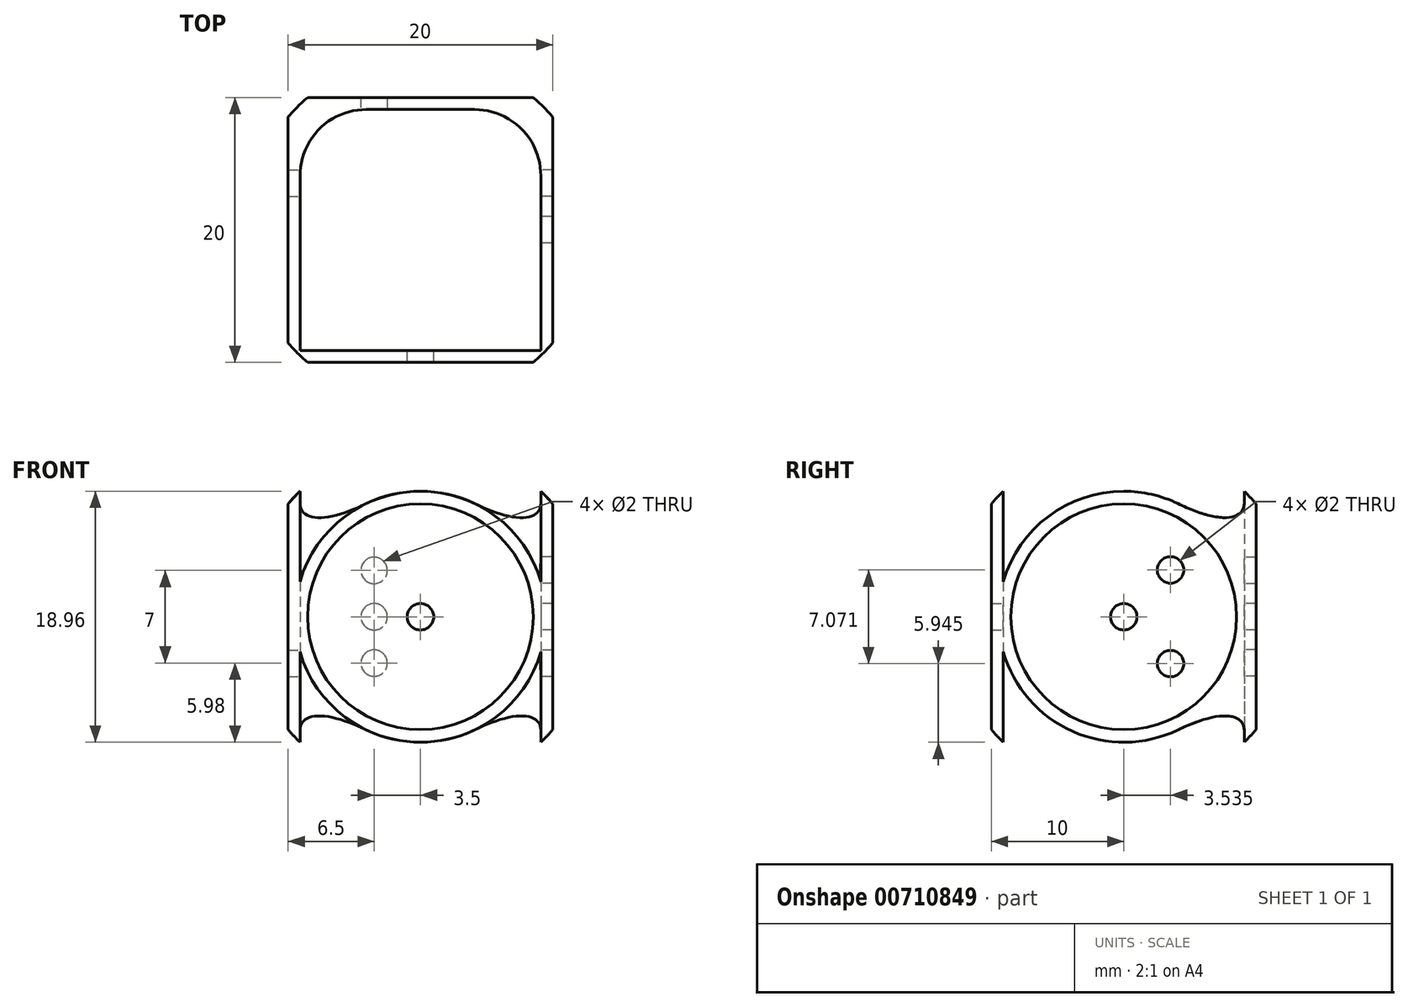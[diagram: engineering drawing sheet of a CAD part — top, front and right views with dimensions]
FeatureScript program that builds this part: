
annotation { "Feature Type Name" : "Feature", "Feature Type Description" : "" }
export const myFeature = defineFeature(function(context is Context, id is Id, definition is map)
    precondition{}
    {
        {
            assignVariable(context, id + "F0", {"name" : "length", "anyValue" : 20 * mm});
        }
        {
            var Q0;
            Q0=qCreatedBy(makeId("Top.planeOp"),FACE);
            var sketch = newSketch(context, id + "F1", { "sketchPlane" : qUnion([Q0])});
            skLineSegment(sketch, "E0.bottom", {"start": v(10, -10) * mm, "end": v(-10, -10) * mm});
            skLineSegment(sketch, "E0.top", {"start": v(10, 10) * mm, "end": v(-10, 10) * mm});
            skLineSegment(sketch, "E0.left", {"start": v(10, -10) * mm, "end": v(10, 10) * mm});
            skLineSegment(sketch, "E0.right", {"start": v(-10, -10) * mm, "end": v(-10, 10) * mm});
            skPoint(sketch, "E0.middle", {"position": v(0, 0) * mm});
            skCircle(sketch, "E1", {"center": v(0, 0) * mm, "radius": 13.14 * mm});
            skCircle(sketch, "E2", {"center": v(0, 0) * mm, "radius": 20 * mm});
            skLineSegment(sketch, "E3", {"start": v(-20, 0) * mm, "end": v(20, 0) * mm});
            skLineSegment(sketch, "E4", {"start": v(-10, 0) * mm, "end": v(-9, 0) * mm, "construction": true});
            skLineSegment(sketch, "E5", {"start": v(9, 0) * mm, "end": v(10, 0) * mm, "construction": true});
            skLineSegment(sketch, "E6.bottom", {"start": v(-9, 0) * mm, "end": v(9, 0) * mm});
            skLineSegment(sketch, "E7", {"start": v(-10, -10) * mm, "end": v(0, 0) * mm, "construction": true});
            skLineSegment(sketch, "E8", {"start": v(0, 0) * mm, "end": v(10, -10) * mm, "construction": true});
            skLineSegment(sketch, "E9.0", {"start": v(4.1, 9.1) * mm, "end": v(-4.1, 9.1) * mm});
            skLineSegment(sketch, "E9.1", {"start": v(9.1, -9.1) * mm, "end": v(9.1, 4.1) * mm});
            skLineSegment(sketch, "E9.2", {"start": v(9.1, -9.1) * mm, "end": v(-9.1, -9.1) * mm});
            skLineSegment(sketch, "E9.3", {"start": v(-9.1, -9.1) * mm, "end": v(-9.1, 4.1) * mm});
            skPoint(sketch, "E10.visualSharp", {"position": v(-9.1, 9.1) * mm});
            skArc(sketch, "E10.filletArc", {"start": v(-4.1, 9.1) * mm, "mid": v(-7.64, 7.64) * mm, "end": v(-9.1, 4.1) * mm});
            skPoint(sketch, "E11.visualSharp", {"position": v(9.1, 9.1) * mm});
            skArc(sketch, "E11.filletArc", {"start": v(9.1, 4.1) * mm, "mid": v(7.64, 7.64) * mm, "end": v(4.1, 9.1) * mm});
            skLineSegment(sketch, "E12.bottom", {"start": v(-9.1, -9.1) * mm, "end": v(9.1, -9.1) * mm});
            skLineSegment(sketch, "E12.top", {"start": v(-9.1, -4) * mm, "end": v(9.1, -4) * mm});
            skLineSegment(sketch, "E12.left", {"start": v(-9.1, -9.1) * mm, "end": v(-9.1, -4) * mm});
            skLineSegment(sketch, "E12.right", {"start": v(9.1, -9.1) * mm, "end": v(9.1, -4) * mm});
            skLineSegment(sketch, "E13.top", {"start": v(-9.1, -2) * mm, "end": v(9.1, -2) * mm});
            skLineSegment(sketch, "E13.left", {"start": v(-9.1, -4) * mm, "end": v(-9.1, -2) * mm});
            skLineSegment(sketch, "E13.right", {"start": v(9.1, -4) * mm, "end": v(9.1, -2) * mm});
            skLineSegment(sketch, "E14", {"start": v(0, 9.1) * mm, "end": v(0, -9.1) * mm});
            skSolve(sketch);
        }
        {
            var Q0;
            Q0=makeQuery(id+"F1.imprint","IMPRINT",FACE,{"disambiguationData":[TD([[makeQuery(id+"F1.imprint","IMPRINT",EDGE,{"derivedFrom":sQuery(id+"F1.wireOp",EDGE,"E0.bottom")}),-1.0]])]});
            var Q1;
            {var subQ0=sQuery(id+"F1.wireOp",EDGE,"Hq5PeDMM-4LUm-VwHA-vir1-N3C3vIOzQR29");var subQ1=sQuery(id+"F1.wireOp",EDGE,"E0.right");var subQ8=makeQuery(id+"F1.imprint","INTERSECT",VERTEX,{"disambiguationData":[OD(0.0)],"derivedFrom":[subQ1,subQ0]});Q1=makeQuery(id+"F1.imprint","IMPRINT",FACE,{"disambiguationData":[TD([[makeQuery(id+"F1.imprint","IMPRINT",EDGE,{"disambiguationData":[TD([[subQ8,-1.0]])],"derivedFrom":subQ1}),-1.0]])]});}
            var Q2;
            {var subQ1=sQuery(id+"F1.wireOp",EDGE,"E0.left");var subQ3=sQuery(id+"F1.wireOp",EDGE,"Hq5PeDMM-4LUm-VwHA-vir1-N3C3vIOzQR29");var subQ4=makeQuery(id+"F1.imprint","INTERSECT",VERTEX,{"disambiguationData":[OD(0.0)],"derivedFrom":[subQ1,subQ3]});Q2=makeQuery(id+"F1.imprint","IMPRINT",FACE,{"disambiguationData":[TD([[makeQuery(id+"F1.imprint","IMPRINT",EDGE,{"disambiguationData":[TD([[subQ4,1.0]])],"derivedFrom":subQ3}),-1.0]])]});}
            var Q3;
            {var subQ0=sQuery(id+"F1.wireOp",EDGE,"Hq5PeDMM-4LUm-VwHA-vir1-N3C3vIOzQR29");var subQ1=sQuery(id+"F1.wireOp",EDGE,"E0.left");var subQ7=makeQuery(id+"F1.imprint","INTERSECT",VERTEX,{"disambiguationData":[OD(0.0)],"derivedFrom":[subQ1,subQ0]});Q3=makeQuery(id+"F1.imprint","IMPRINT",FACE,{"disambiguationData":[TD([[makeQuery(id+"F1.imprint","IMPRINT",EDGE,{"disambiguationData":[TD([[subQ7,-1.0]])],"derivedFrom":subQ1}),1.0]])]});}
            var Q4;
            {var subQ1=sQuery(id+"F1.wireOp",EDGE,"E0.right");var subQ3=sQuery(id+"F1.wireOp",EDGE,"Hq5PeDMM-4LUm-VwHA-vir1-N3C3vIOzQR29");var subQ4=makeQuery(id+"F1.imprint","INTERSECT",VERTEX,{"disambiguationData":[OD(0.0)],"derivedFrom":[subQ1,subQ3]});Q4=makeQuery(id+"F1.imprint","IMPRINT",FACE,{"disambiguationData":[TD([[makeQuery(id+"F1.imprint","IMPRINT",EDGE,{"disambiguationData":[TD([[subQ4,-1.0]])],"derivedFrom":subQ3}),-1.0]])]});}
            var Q5;
            {var subQ0=sQuery(id+"F1.wireOp",EDGE,"Hq5PeDMM-4LUm-VwHA-vir1-N3C3vIOzQR29");var subQ1=sQuery(id+"F1.wireOp",EDGE,"E0.top");var subQ2=makeQuery(id+"F1.imprint","INTERSECT",VERTEX,{"disambiguationData":[OD(0.0)],"derivedFrom":[subQ1,subQ0]});Q5=makeQuery(id+"F1.imprint","IMPRINT",FACE,{"disambiguationData":[TD([[makeQuery(id+"F1.imprint","IMPRINT",EDGE,{"disambiguationData":[TD([[subQ2,-1.0]])],"derivedFrom":subQ1}),1.0]])]});}
            var Q6;
            {var subQ1=sQuery(id+"F1.wireOp",EDGE,"E0.top");var subQ3=sQuery(id+"F1.wireOp",EDGE,"Hq5PeDMM-4LUm-VwHA-vir1-N3C3vIOzQR29");var subQ4=makeQuery(id+"F1.imprint","INTERSECT",VERTEX,{"disambiguationData":[OD(1.0)],"derivedFrom":[subQ1,subQ3]});Q6=makeQuery(id+"F1.imprint","IMPRINT",FACE,{"disambiguationData":[TD([[makeQuery(id+"F1.imprint","IMPRINT",EDGE,{"disambiguationData":[TD([[subQ4,-1.0]])],"derivedFrom":subQ3}),-1.0]])]});}
            var Q7;
            {var subQ1=sQuery(id+"F1.wireOp",EDGE,"E0.right");var subQ3=sQuery(id+"F1.wireOp",EDGE,"Hq5PeDMM-4LUm-VwHA-vir1-N3C3vIOzQR29");var subQ4=makeQuery(id+"F1.imprint","INTERSECT",VERTEX,{"disambiguationData":[OD(1.0)],"derivedFrom":[subQ1,subQ3]});Q7=makeQuery(id+"F1.imprint","IMPRINT",FACE,{"disambiguationData":[TD([[makeQuery(id+"F1.imprint","IMPRINT",EDGE,{"disambiguationData":[TD([[subQ4,1.0]])],"derivedFrom":subQ3}),-1.0]])]});}
            var Q8;
            {var subQ1=sQuery(id+"F1.wireOp",EDGE,"E0.top");var subQ3=sQuery(id+"F1.wireOp",EDGE,"Hq5PeDMM-4LUm-VwHA-vir1-N3C3vIOzQR29");var subQ4=makeQuery(id+"F1.imprint","INTERSECT",VERTEX,{"disambiguationData":[OD(0.0)],"derivedFrom":[subQ1,subQ3]});Q8=makeQuery(id+"F1.imprint","IMPRINT",FACE,{"disambiguationData":[TD([[makeQuery(id+"F1.imprint","IMPRINT",EDGE,{"disambiguationData":[TD([[subQ4,1.0]])],"derivedFrom":subQ3}),-1.0]])]});}
            var Q9;
            {var subQ1=sQuery(id+"F1.wireOp",EDGE,"E0.left");var subQ3=sQuery(id+"F1.wireOp",EDGE,"Hq5PeDMM-4LUm-VwHA-vir1-N3C3vIOzQR29");var subQ4=makeQuery(id+"F1.imprint","INTERSECT",VERTEX,{"disambiguationData":[OD(1.0)],"derivedFrom":[subQ1,subQ3]});Q9=makeQuery(id+"F1.imprint","IMPRINT",FACE,{"disambiguationData":[TD([[makeQuery(id+"F1.imprint","IMPRINT",EDGE,{"disambiguationData":[TD([[subQ4,-1.0]])],"derivedFrom":subQ3}),-1.0]])]});}
            var Q10;
            {var subQ0=sQuery(id+"F1.wireOp",EDGE,"Hq5PeDMM-4LUm-VwHA-vir1-N3C3vIOzQR29");var subQ1=sQuery(id+"F1.wireOp",EDGE,"E0.bottom");var subQ8=makeQuery(id+"F1.imprint","INTERSECT",VERTEX,{"disambiguationData":[OD(0.0)],"derivedFrom":[subQ1,subQ0]});Q10=makeQuery(id+"F1.imprint","IMPRINT",FACE,{"disambiguationData":[TD([[makeQuery(id+"F1.imprint","IMPRINT",EDGE,{"disambiguationData":[TD([[subQ8,-1.0]])],"derivedFrom":subQ1}),-1.0]])]});}
            var Q11;
            {var subQ0=sQuery(id+"F1.wireOp",EDGE,"E1");var subQ1=sQuery(id+"F1.wireOp",EDGE,"E0.bottom");var subQ10=makeQuery(id+"F1.imprint","INTERSECT",VERTEX,{"disambiguationData":[OD(0.0)],"derivedFrom":[subQ1,subQ0]});Q11=makeQuery(id+"F1.imprint","IMPRINT",FACE,{"disambiguationData":[TD([[makeQuery(id+"F1.imprint","IMPRINT",EDGE,{"disambiguationData":[TD([[subQ10,-1.0]])],"derivedFrom":subQ1}),-1.0]])]});}
            var Q12;
            {var subQ0=sQuery(id+"F1.wireOp",EDGE,"E1");var subQ1=sQuery(id+"F1.wireOp",EDGE,"E0.top");var subQ2=makeQuery(id+"F1.imprint","INTERSECT",VERTEX,{"disambiguationData":[OD(0.0)],"derivedFrom":[subQ1,subQ0]});Q12=makeQuery(id+"F1.imprint","IMPRINT",FACE,{"disambiguationData":[TD([[makeQuery(id+"F1.imprint","IMPRINT",EDGE,{"disambiguationData":[TD([[subQ2,-1.0]])],"derivedFrom":subQ1}),1.0]])]});}
            var Q13;
            {var subQ0=sQuery(id+"F1.wireOp",EDGE,"E0.right");var subQ1=sQuery(id+"F1.wireOp",EDGE,"E0.top");var subQ2=makeQuery(id+"F1.imprint","INTERSECT",VERTEX,{"derivedFrom":[subQ1,subQ0]});Q13=makeQuery(id+"F1.imprint","IMPRINT",FACE,{"disambiguationData":[TD([[makeQuery(id+"F1.imprint","IMPRINT",EDGE,{"disambiguationData":[TD([[subQ2,1.0]])],"derivedFrom":subQ1}),1.0]])]});}
            var Q14;
            {var subQ0=sQuery(id+"F1.wireOp",EDGE,"E0.left");var subQ1=sQuery(id+"F1.wireOp",EDGE,"E0.top");var subQ2=makeQuery(id+"F1.imprint","INTERSECT",VERTEX,{"derivedFrom":[subQ1,subQ0]});Q14=makeQuery(id+"F1.imprint","IMPRINT",FACE,{"disambiguationData":[TD([[makeQuery(id+"F1.imprint","IMPRINT",EDGE,{"disambiguationData":[TD([[subQ2,-1.0]])],"derivedFrom":subQ1}),1.0]])]});}
            var Q15;
            {var subQ0=sQuery(id+"F1.wireOp",EDGE,"patfPrjC-I4Qt-dAkN-TGbB-FqZXeeQMi0Ai");Q15=makeQuery(id+"F1.imprint","IMPRINT",FACE,{"disambiguationData":[TD([[makeQuery(id+"F1.imprint","IMPRINT",EDGE,{"derivedFrom":subQ0}),1.0]])]});}
            var Q16;
            Q16=makeQuery(id+"F1.imprint","IMPRINT",FACE,{"disambiguationData":[TD([[makeQuery(id+"F1.imprint","IMPRINT",EDGE,{"derivedFrom":sQuery(id+"F1.wireOp",EDGE,"E6.bottom")}),1.0]])]});
            var Q17;
            Q17=makeQuery(id+"F1.imprint","IMPRINT",FACE,{"disambiguationData":[TD([[makeQuery(id+"F1.imprint","IMPRINT",EDGE,{"derivedFrom":sQuery(id+"F1.wireOp",EDGE,"E6.bottom")}),-1.0]])]});
            var Q18;
            {var subQ0=sQuery(id+"F1.wireOp",EDGE,"iiYfwUfe-HNib-MqOO-iY6M-OHTfmbP10WrW");var subQ5=sQuery(id+"F1.wireOp",EDGE,"jVtNNkBl-UzNA-jzoa-2J3p-JG0xdHmN4cFF");var subQ6=makeQuery(id+"F1.imprint","INTERSECT",VERTEX,{"derivedFrom":[subQ0,subQ5]});Q18=makeQuery(id+"F1.imprint","IMPRINT",FACE,{"disambiguationData":[TD([[makeQuery(id+"F1.imprint","IMPRINT",EDGE,{"disambiguationData":[TD([[subQ6,1.0]])],"derivedFrom":subQ5}),-1.0]])]});}
            var Q19;
            {var subQ0=sQuery(id+"F1.wireOp",EDGE,"E6.left");Q19=makeQuery(id+"F1.imprint","IMPRINT",FACE,{"disambiguationData":[TD([[makeQuery(id+"F1.imprint","IMPRINT",EDGE,{"derivedFrom":subQ0}),-1.0]])]});}
            var Q20;
            {var subQ1=sQuery(id+"F1.wireOp",EDGE,"E6.right");Q20=makeQuery(id+"F1.imprint","IMPRINT",FACE,{"disambiguationData":[TD([[makeQuery(id+"F1.imprint","IMPRINT",EDGE,{"derivedFrom":subQ1}),1.0]])]});}
            var Q21;
            {var subQ0=sQuery(id+"F1.wireOp",EDGE,"iiYfwUfe-HNib-MqOO-iY6M-OHTfmbP10WrW");var subQ5=sQuery(id+"F1.wireOp",EDGE,"jVtNNkBl-UzNA-jzoa-2J3p-JG0xdHmN4cFF");var subQ6=makeQuery(id+"F1.imprint","INTERSECT",VERTEX,{"derivedFrom":[subQ0,subQ5]});Q21=makeQuery(id+"F1.imprint","IMPRINT",FACE,{"disambiguationData":[TD([[makeQuery(id+"F1.imprint","IMPRINT",EDGE,{"disambiguationData":[TD([[subQ6,1.0]])],"derivedFrom":subQ5}),1.0]])]});}
            var Q22;
            Q22=makeQuery(id+"F1.imprint","IMPRINT",FACE,{"disambiguationData":[TD([[makeQuery(id+"F1.imprint","IMPRINT",EDGE,{"derivedFrom":sQuery(id+"F1.wireOp",EDGE,"E12.bottom")}),1.0]])]});
            var Q23;
            {var subQ0=sQuery(id+"F1.wireOp",EDGE,"E13.left");Q23=makeQuery(id+"F1.imprint","IMPRINT",FACE,{"disambiguationData":[TD([[makeQuery(id+"F1.imprint","IMPRINT",EDGE,{"derivedFrom":subQ0}),-1.0]])]});}
            var Q24;
            {var subQ0=sQuery(id+"F1.wireOp",EDGE,"E13.right");Q24=makeQuery(id+"F1.imprint","IMPRINT",FACE,{"disambiguationData":[TD([[makeQuery(id+"F1.imprint","IMPRINT",EDGE,{"derivedFrom":subQ0}),1.0]])]});}
            extrude(context, id + "F2", {"entities" : qUnion([Q0, Q1, Q2, Q3, Q4, Q5, Q6, Q7, Q8, Q9, Q10, Q11, Q12, Q13, Q14, Q15, Q16, Q17, Q18, Q19, Q20, Q21, Q22, Q23, Q24]), "endBound" : BoundingType.SYMMETRIC, "depth" : getVariable(context, 'length'), "offsetDistance" : 25 * mm});
        }
        {
            var Q0;
            {var subQ0=sQuery(id+"F1.wireOp",EDGE,"E0.right");var subQ1=sQuery(id+"F1.wireOp",EDGE,"E0.top");var subQ2=makeQuery(id+"F1.imprint","INTERSECT",VERTEX,{"derivedFrom":[subQ1,subQ0]});Q0=makeQuery(id+"F1.imprint","IMPRINT",FACE,{"disambiguationData":[TD([[makeQuery(id+"F1.imprint","IMPRINT",EDGE,{"disambiguationData":[TD([[subQ2,1.0]])],"derivedFrom":subQ1}),1.0]])]});}
            var Q1;
            {var subQ0=sQuery(id+"F1.wireOp",EDGE,"E0.left");var subQ1=sQuery(id+"F1.wireOp",EDGE,"E0.top");var subQ2=makeQuery(id+"F1.imprint","INTERSECT",VERTEX,{"derivedFrom":[subQ1,subQ0]});Q1=makeQuery(id+"F1.imprint","IMPRINT",FACE,{"disambiguationData":[TD([[makeQuery(id+"F1.imprint","IMPRINT",EDGE,{"disambiguationData":[TD([[subQ2,-1.0]])],"derivedFrom":subQ1}),-1.0]])]});}
            var Q2;
            {var subQ0=sQuery(id+"F1.wireOp",EDGE,"E0.left");var subQ1=sQuery(id+"F1.wireOp",EDGE,"E0.top");var subQ2=makeQuery(id+"F1.imprint","INTERSECT",VERTEX,{"derivedFrom":[subQ1,subQ0]});Q2=makeQuery(id+"F1.imprint","IMPRINT",FACE,{"disambiguationData":[TD([[makeQuery(id+"F1.imprint","IMPRINT",EDGE,{"disambiguationData":[TD([[subQ2,-1.0]])],"derivedFrom":subQ1}),1.0]])]});}
            var Q3;
            Q3=sQuery(id+"F1.wireOp",EDGE,"E3");
            revolve(context, id + "F3", {"operationType" : NewBodyOperationType.REMOVE, "surfaceOperationType" : NewSurfaceOperationType.NEW, "entities" : qUnion([Q0, Q1, Q2]), "axis" : qUnion([Q3]), "revolveType" : RevolveType.FULL, "oppositeDirection" : true});
        }
        {
            var Q0;
            {var subQ0=sQuery(id+"F1.wireOp",EDGE,"E10.filletArc");Q0=makeQuery(id+"F1.imprint","IMPRINT",FACE,{"disambiguationData":[TD([[makeQuery(id+"F1.imprint","IMPRINT",EDGE,{"derivedFrom":subQ0}),1.0]])]});}
            var Q1;
            {var subQ5=sQuery(id+"F1.wireOp",EDGE,"E3");var subQ7=sQuery(id+"F1.wireOp",EDGE,"E6.bottom");var subQ8=makeQuery(id+"F1.imprint","INTERSECT",VERTEX,{"disambiguationData":[OD(0.0)],"derivedFrom":[subQ5,subQ7]});Q1=makeQuery(id+"F1.imprint","IMPRINT",FACE,{"disambiguationData":[TD([[makeQuery(id+"F1.imprint","IMPRINT",EDGE,{"disambiguationData":[TD([[subQ8,1.0]])],"derivedFrom":subQ5}),-1.0]])]});}
            var Q2;
            {var subQ0=sQuery(id+"F1.wireOp",EDGE,"E12.left");Q2=makeQuery(id+"F1.imprint","IMPRINT",FACE,{"disambiguationData":[TD([[makeQuery(id+"F1.imprint","IMPRINT",EDGE,{"derivedFrom":subQ0}),-1.0]])]});}
            var Q3;
            Q3=sQuery(id+"F1.wireOp",EDGE,"E14");
            revolve(context, id + "F4", {"operationType" : NewBodyOperationType.REMOVE, "surfaceOperationType" : NewSurfaceOperationType.NEW, "entities" : qUnion([Q0, Q1, Q2]), "axis" : qUnion([Q3]), "revolveType" : RevolveType.FULL, "oppositeDirection" : true});
        }
        {
            var Q0;
            Q0=qCreatedBy(makeId("Front.planeOp"),FACE);
            var sketch = newSketch(context, id + "F5", { "sketchPlane" : qUnion([Q0])});
            skCircle(sketch, "E15", {"center": v(-3.5, 0) * mm, "radius": 1 * mm});
            skCircle(sketch, "E16", {"center": v(-3.5, 3.5) * mm, "radius": 1 * mm});
            skCircle(sketch, "E17", {"center": v(-3.5, -3.5) * mm, "radius": 1 * mm});
            skLineSegment(sketch, "E18", {"start": v(-3.5, 3.5) * mm, "end": v(-3.5, 0) * mm, "construction": true});
            skLineSegment(sketch, "E19", {"start": v(-3.5, 0) * mm, "end": v(-3.5, -3.5) * mm, "construction": true});
            skLineSegment(sketch, "E20", {"start": v(-3.5, 0) * mm, "end": v(0, 0) * mm, "construction": true});
            skCircle(sketch, "E21.MirrorC", {"center": v(3.5, 3.5) * mm, "radius": 1 * mm});
            skCircle(sketch, "E22.MirrorC", {"center": v(3.5, 0) * mm, "radius": 1 * mm});
            skCircle(sketch, "E23.MirrorC", {"center": v(3.5, -3.5) * mm, "radius": 1 * mm});
            skCircle(sketch, "E24", {"center": v(0, 0) * mm, "radius": 1 * mm});
            skSolve(sketch);
        }
        {
            var Q0;
            Q0=makeQuery(id+"F5.imprint","IMPRINT",FACE,{"disambiguationData":[TD([[makeQuery(id+"F5.imprint","IMPRINT",EDGE,{"derivedFrom":sQuery(id+"F5.wireOp",EDGE,"E16")}),1.0]])]});
            var Q1;
            Q1=makeQuery(id+"F5.imprint","IMPRINT",FACE,{"disambiguationData":[TD([[makeQuery(id+"F5.imprint","IMPRINT",EDGE,{"derivedFrom":sQuery(id+"F5.wireOp",EDGE,"E15")}),1.0]])]});
            var Q2;
            Q2=makeQuery(id+"F5.imprint","IMPRINT",FACE,{"disambiguationData":[TD([[makeQuery(id+"F5.imprint","IMPRINT",EDGE,{"derivedFrom":sQuery(id+"F5.wireOp",EDGE,"E17")}),1.0]])]});
            var Q3;
            Q3=makeQuery(id+"F5.imprint","IMPRINT",FACE,{"disambiguationData":[TD([[makeQuery(id+"F5.imprint","IMPRINT",EDGE,{"derivedFrom":sQuery(id+"F5.wireOp",EDGE,"E23.MirrorC")}),-1.0]])]});
            var Q4;
            Q4=makeQuery(id+"F5.imprint","IMPRINT",FACE,{"disambiguationData":[TD([[makeQuery(id+"F5.imprint","IMPRINT",EDGE,{"derivedFrom":sQuery(id+"F5.wireOp",EDGE,"E22.MirrorC")}),-1.0]])]});
            var Q5;
            Q5=makeQuery(id+"F5.imprint","IMPRINT",FACE,{"disambiguationData":[TD([[makeQuery(id+"F5.imprint","IMPRINT",EDGE,{"derivedFrom":sQuery(id+"F5.wireOp",EDGE,"E21.MirrorC")}),-1.0]])]});
            extrude(context, id + "F6", {"entities" : qUnion([Q0, Q1, Q2, Q3, Q4, Q5]), "operationType" : NewBodyOperationType.REMOVE, "oppositeDirection" : true, "depth" : 25 * mm, "offsetDistance" : 25 * mm});
        }
        {
            var Q0;
            Q0=makeQuery(id+"F5.imprint","IMPRINT",FACE,{"disambiguationData":[TD([[makeQuery(id+"F5.imprint","IMPRINT",EDGE,{"derivedFrom":sQuery(id+"F5.wireOp",EDGE,"E24")}),1.0]])]});
            extrude(context, id + "F7", {"entities" : qUnion([Q0]), "operationType" : NewBodyOperationType.REMOVE, "depth" : 25 * mm, "offsetDistance" : 25 * mm});
        }
        {
            var Q0;
            Q0=qCreatedBy(makeId("Right.planeOp"),FACE);
            var sketch = newSketch(context, id + "F8", { "sketchPlane" : qUnion([Q0])});
            skCircle(sketch, "E25", {"center": v(0, 0) * mm, "radius": 1 * mm});
            skCircle(sketch, "E26", {"center": v(3.54, 3.54) * mm, "radius": 1 * mm});
            skCircle(sketch, "E27", {"center": v(3.54, -3.54) * mm, "radius": 1 * mm});
            skLineSegment(sketch, "E28", {"start": v(0, 0) * mm, "end": v(3.54, 3.54) * mm, "construction": true});
            skLineSegment(sketch, "E29", {"start": v(0, 0) * mm, "end": v(3.54, -3.54) * mm, "construction": true});
            skCircle(sketch, "E30.MirrorC", {"center": v(-3.54, 3.54) * mm, "radius": 1 * mm});
            skCircle(sketch, "E31.MirrorC", {"center": v(-3.54, -3.54) * mm, "radius": 1 * mm});
            skSolve(sketch);
        }
        {
            var Q0;
            Q0=makeQuery(id+"F8.imprint","IMPRINT",FACE,{"disambiguationData":[TD([[makeQuery(id+"F8.imprint","IMPRINT",EDGE,{"derivedFrom":sQuery(id+"F8.wireOp",EDGE,"E30.MirrorC")}),-1.0]])]});
            var Q1;
            Q1=makeQuery(id+"F8.imprint","IMPRINT",FACE,{"disambiguationData":[TD([[makeQuery(id+"F8.imprint","IMPRINT",EDGE,{"derivedFrom":sQuery(id+"F8.wireOp",EDGE,"E25")}),1.0]])]});
            var Q2;
            Q2=makeQuery(id+"F8.imprint","IMPRINT",FACE,{"disambiguationData":[TD([[makeQuery(id+"F8.imprint","IMPRINT",EDGE,{"derivedFrom":sQuery(id+"F8.wireOp",EDGE,"E27")}),1.0]])]});
            var Q3;
            Q3=makeQuery(id+"F8.imprint","IMPRINT",FACE,{"disambiguationData":[TD([[makeQuery(id+"F8.imprint","IMPRINT",EDGE,{"derivedFrom":sQuery(id+"F8.wireOp",EDGE,"E26")}),1.0]])]});
            var Q4;
            Q4=makeQuery(id+"F8.imprint","IMPRINT",FACE,{"disambiguationData":[TD([[makeQuery(id+"F8.imprint","IMPRINT",EDGE,{"derivedFrom":sQuery(id+"F8.wireOp",EDGE,"E31.MirrorC")}),-1.0]])]});
            extrude(context, id + "F9", {"entities" : qUnion([Q0, Q1, Q2, Q3, Q4]), "operationType" : NewBodyOperationType.REMOVE, "depth" : 25 * mm, "offsetDistance" : 25 * mm});
        }
        {
            var Q0;
            Q0=makeQuery(id+"F8.imprint","IMPRINT",FACE,{"disambiguationData":[TD([[makeQuery(id+"F8.imprint","IMPRINT",EDGE,{"derivedFrom":sQuery(id+"F8.wireOp",EDGE,"E30.MirrorC")}),-1.0]])]});
            var Q1;
            Q1=makeQuery(id+"F8.imprint","IMPRINT",FACE,{"disambiguationData":[TD([[makeQuery(id+"F8.imprint","IMPRINT",EDGE,{"derivedFrom":sQuery(id+"F8.wireOp",EDGE,"E27")}),1.0]])]});
            extrude(context, id + "F10", {"entities" : qUnion([Q0, Q1]), "operationType" : NewBodyOperationType.REMOVE, "oppositeDirection" : true, "depth" : 25 * mm, "offsetDistance" : 25 * mm});
        }
        {
            var Q0;
            Q0=qCreatedBy(makeId("Top.planeOp"),FACE);
            var sketch = newSketch(context, id + "F11", { "sketchPlane" : qUnion([Q0])});
            skCircle(sketch, "E32", {"center": v(0, 0) * mm, "radius": 1 * mm});
            skCircle(sketch, "E33", {"center": v(3.54, 3.54) * mm, "radius": 1 * mm});
            skCircle(sketch, "E34", {"center": v(3.54, -3.54) * mm, "radius": 1 * mm});
            skLineSegment(sketch, "E35", {"start": v(0, 0) * mm, "end": v(3.54, 3.54) * mm, "construction": true});
            skLineSegment(sketch, "E36", {"start": v(0, 0) * mm, "end": v(3.54, -3.54) * mm, "construction": true});
            skCircle(sketch, "E37.MirrorC", {"center": v(-3.54, -3.54) * mm, "radius": 1 * mm});
            skCircle(sketch, "E38.MirrorC", {"center": v(-3.54, 3.54) * mm, "radius": 1 * mm});
            skSolve(sketch);
        }
        {
            var Q0;
            Q0=makeQuery(id+"F11.imprint","IMPRINT",FACE,{"disambiguationData":[TD([[makeQuery(id+"F11.imprint","IMPRINT",EDGE,{"derivedFrom":sQuery(id+"F11.wireOp",EDGE,"E37.MirrorC")}),-1.0]])]});
            var Q1;
            Q1=makeQuery(id+"F11.imprint","IMPRINT",FACE,{"disambiguationData":[TD([[makeQuery(id+"F11.imprint","IMPRINT",EDGE,{"derivedFrom":sQuery(id+"F11.wireOp",EDGE,"E34")}),1.0]])]});
            var Q2;
            Q2=makeQuery(id+"F11.imprint","IMPRINT",FACE,{"disambiguationData":[TD([[makeQuery(id+"F11.imprint","IMPRINT",EDGE,{"derivedFrom":sQuery(id+"F11.wireOp",EDGE,"E33")}),1.0]])]});
            var Q3;
            Q3=makeQuery(id+"F11.imprint","IMPRINT",FACE,{"disambiguationData":[TD([[makeQuery(id+"F11.imprint","IMPRINT",EDGE,{"derivedFrom":sQuery(id+"F11.wireOp",EDGE,"E38.MirrorC")}),-1.0]])]});
            extrude(context, id + "F12", {"entities" : qUnion([Q0, Q1, Q2, Q3]), "operationType" : NewBodyOperationType.REMOVE, "oppositeDirection" : true, "depth" : 25 * mm, "offsetDistance" : 25 * mm});
        }
        {
            var Q0;
            Q0=makeQuery(id+"F11.imprint","IMPRINT",FACE,{"disambiguationData":[TD([[makeQuery(id+"F11.imprint","IMPRINT",EDGE,{"derivedFrom":sQuery(id+"F11.wireOp",EDGE,"E37.MirrorC")}),-1.0]])]});
            var Q1;
            Q1=makeQuery(id+"F11.imprint","IMPRINT",FACE,{"disambiguationData":[TD([[makeQuery(id+"F11.imprint","IMPRINT",EDGE,{"derivedFrom":sQuery(id+"F11.wireOp",EDGE,"E32")}),1.0]])]});
            var Q2;
            Q2=makeQuery(id+"F11.imprint","IMPRINT",FACE,{"disambiguationData":[TD([[makeQuery(id+"F11.imprint","IMPRINT",EDGE,{"derivedFrom":sQuery(id+"F11.wireOp",EDGE,"E33")}),1.0]])]});
            extrude(context, id + "F13", {"entities" : qUnion([Q0, Q1, Q2]), "operationType" : NewBodyOperationType.REMOVE, "depth" : 25 * mm, "offsetDistance" : 25 * mm});
        }
    });
